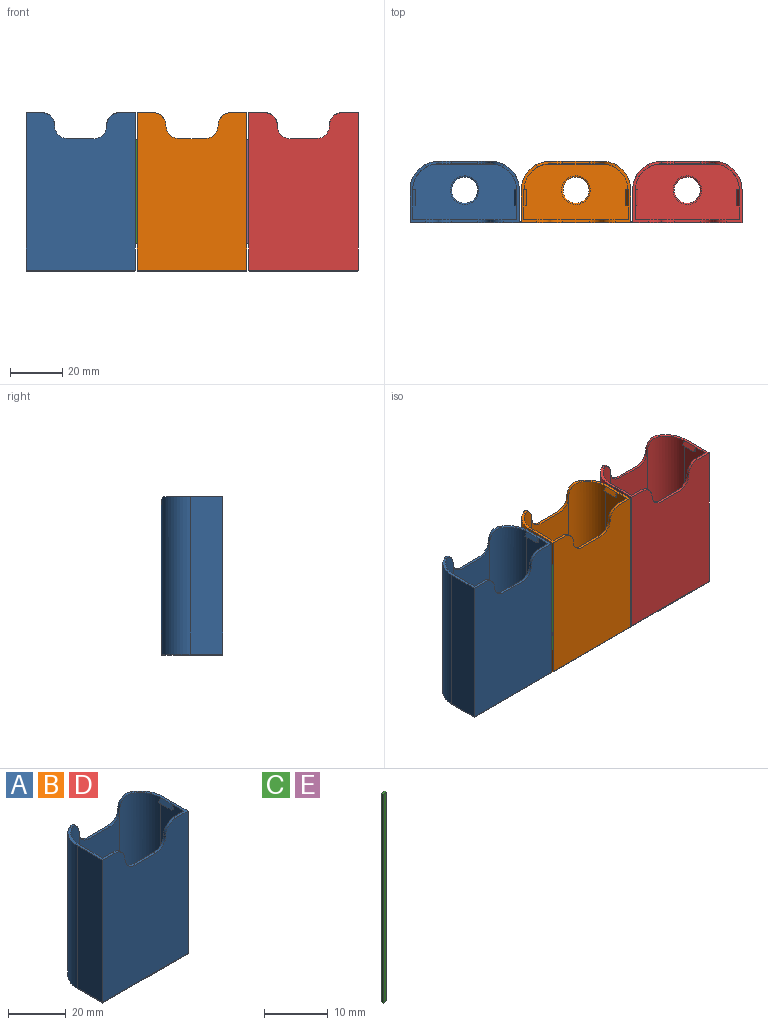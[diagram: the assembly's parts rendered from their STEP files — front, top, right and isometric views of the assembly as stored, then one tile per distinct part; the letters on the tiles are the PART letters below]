
ASSEMBLY  parts=5 mates=4
PART A: 41 faces, bbox 43.8x24.4x61 mm
  f0: plane 55.5x20mm, normal (0,1,0), area 1020.7mm2, adj f4,f8,f17,f22,f24,f27
  f1: plane 22.3x6mm, normal (0,0,1), area 28.8mm2, adj f3,f6,f7,f8,f13,f14,f21,f25
  f2: plane 55x20mm, normal (0,-1,0), area 1010.7mm2, adj f11,f14,f15,f17,f22,f24
  f3: plane 60x40mm, normal (0,1,0), area 2200mm2, adj f1,f9,f12,f13,f15,f16,f18,f19
  f4: cylinder r=11mm len=60.5mm, axis (0,0,-1), area 1040mm2, adj f0,f5,f9,f23,f29
  f5: plane 60.5x12.5mm, normal (-1,0,0), area 756.2mm2, adj f4,f6,f9,f31
  f6: plane 60.5x42mm, normal (0,-1,0), area 2341mm2, adj f1,f5,f7,f9,f16,f18,f19,f20
  f7: plane 60.5x12.5mm, normal (1,0,0), area 756.2mm2, adj f1,f6,f8,f28
  f8: cylinder r=11mm len=60.5mm, axis (0,0,-1), area 1040mm2, adj f0,f1,f7,f25,f26
  f9: plane 22.3x6mm, normal (0,0,1), area 28.8mm2, adj f3,f4,f5,f6,f11,f12,f19,f23
  f10: plane 41x22.5mm, normal (0,0,-1), area 780.1mm2, adj f26,f27,f28,f29,f30,f31,f32
  f11: cylinder r=10mm len=60mm, axis (0,0,-1), area 937.1mm2, adj f2,f9,f12,f15,f23,f35
  f12: plane 60x11.5mm, normal (1,0,0), area 677.6mm2, adj f3,f9,f11,f15,f33,f34
  f13: plane 60x11.5mm, normal (-1,0,0), area 677.6mm2, adj f1,f3,f14,f15,f37,f38
  f14: cylinder r=10mm len=60mm, axis (0,0,-1), area 937.1mm2, adj f1,f2,f13,f15,f25,f39
  f15: plane 40x21.5mm, normal (0,0,1), area 722mm2, adj f2,f3,f11,f12,f13,f14,f32
  f16: plane 10x1mm, normal (0,0,1), area 10mm2, adj f3,f6,f18,f20
  f17: plane 10x1mm, normal (0,0,1), area 10mm2, adj f0,f2,f22,f24
  f18: cylinder r=5mm len=5mm, axis (0,-1,0), area 7.9mm2, adj f3,f6,f16,f19
  f19: cylinder r=5mm len=5mm, axis (0,1,0), area 7.9mm2, adj f3,f6,f9,f18
  f20: cylinder r=5mm len=5mm, axis (0,1,0), area 7.9mm2, adj f3,f6,f16,f21
  f21: cylinder r=5mm len=5mm, axis (0,-1,0), area 7.9mm2, adj f1,f3,f6,f20
  f22: cylinder r=5mm len=5mm, axis (0,-1,0), area 7.9mm2, adj f0,f2,f17,f23
  f23: cylinder r=5mm len=5mm, axis (0,1,0), area 8.1mm2, adj f4,f9,f11,f22
  f24: cylinder r=5mm len=5mm, axis (0,1,0), area 7.9mm2, adj f0,f2,f17,f25
  f25: cylinder r=5mm len=5mm, axis (0,-1,0), area 8.1mm2, adj f1,f8,f14,f24
  f26: torus R=10.5mm, axis (0,0,1), area 13.3mm2, adj f8,f10,f27,f28
  f27: cylinder r=0.5mm len=20mm, axis (-1,0,0), area 15.7mm2, adj f0,f10,f26,f29
  f28: cylinder r=0.5mm len=12.5mm, axis (0,1,0), area 9.7mm2, adj f7,f10,f26,f30
  f29: torus R=10.5mm, axis (0,0,1), area 13.3mm2, adj f4,f10,f27,f31
  f30: cylinder r=0.5mm len=42mm, axis (1,0,0), area 32.7mm2, adj f6,f10,f28,f31
  f31: cylinder r=0.5mm len=12.5mm, axis (0,-1,0), area 9.7mm2, adj f5,f10,f29,f30
  f32: torus R=5.5mm, axis (0,0,1), area 51.1mm2, adj f10,f15
  f33: plane 2x1mm, normal (0,-1,0), area 1mm2, adj f12,f34,f36
  f34: cylinder r=2mm len=6.18mm, axis (0,1,0), area 6.5mm2, adj f12,f33,f35,f36
  f35: plane 2x1mm, normal (0,1,0), area 1mm2, adj f11,f34,f36
  f36: plane 6.18x1.73mm, normal (0.87,0,0.5), area 12.4mm2, adj f9,f33,f34,f35
  f37: plane 2x1mm, normal (0,-1,0), area 1mm2, adj f13,f38,f40
  f38: cylinder r=2mm len=6.18mm, axis (0,1,0), area 6.5mm2, adj f13,f37,f39,f40
  f39: plane 2x1mm, normal (0,1,0), area 1mm2, adj f14,f38,f40
  f40: plane 6.18x1.73mm, normal (-0.87,0,0.5), area 12.4mm2, adj f1,f37,f38,f39
PART B: same geometry as A
PART C: 6 faces, bbox 0.8x0.4x40 mm
  f0: plane 40x0.4mm, normal (1,0,0), area 16mm2, adj f1,f3,f4,f5
  f1: plane 40x0.8mm, normal (0,1,0), area 32mm2, adj f0,f2,f4,f5
  f2: plane 40x0.4mm, normal (-1,0,0), area 16mm2, adj f1,f3,f4,f5
  f3: plane 40x0.8mm, normal (0,-1,0), area 32mm2, adj f0,f2,f4,f5
  f4: plane 0.8x0.4mm, normal (0,0,1), area 0.3mm2, adj f0,f1,f2,f3
  f5: plane 0.8x0.4mm, normal (0,0,-1), area 0.3mm2, adj f0,f1,f2,f3
PART D: same geometry as A
PART E: same geometry as C
PLACE A t=(-63.89,-25.43,-18.08)mm
PLACE B t=(-21.09,-25.43,-18.08)mm
PLACE C t=(-42.49,-31.55,-8.33)mm
PLACE D t=(21.71,-25.43,-18.08)mm
PLACE E t=(0.31,-31.55,-8.33)mm
MATE fastened A.f7 <-> C.f2  axis (1,0,0) through (-42.89,-31.55,11.67)mm
MATE fastened B.f7 <-> E.f2  axis (1,0,0) through (-0.09,-31.55,11.67)mm
MATE fastened C.f0 <-> B.f5  axis (1,0,0) through (-42.09,-31.55,11.67)mm
MATE fastened E.f0 <-> D.f5  axis (1,0,0) through (0.71,-31.55,11.67)mm
